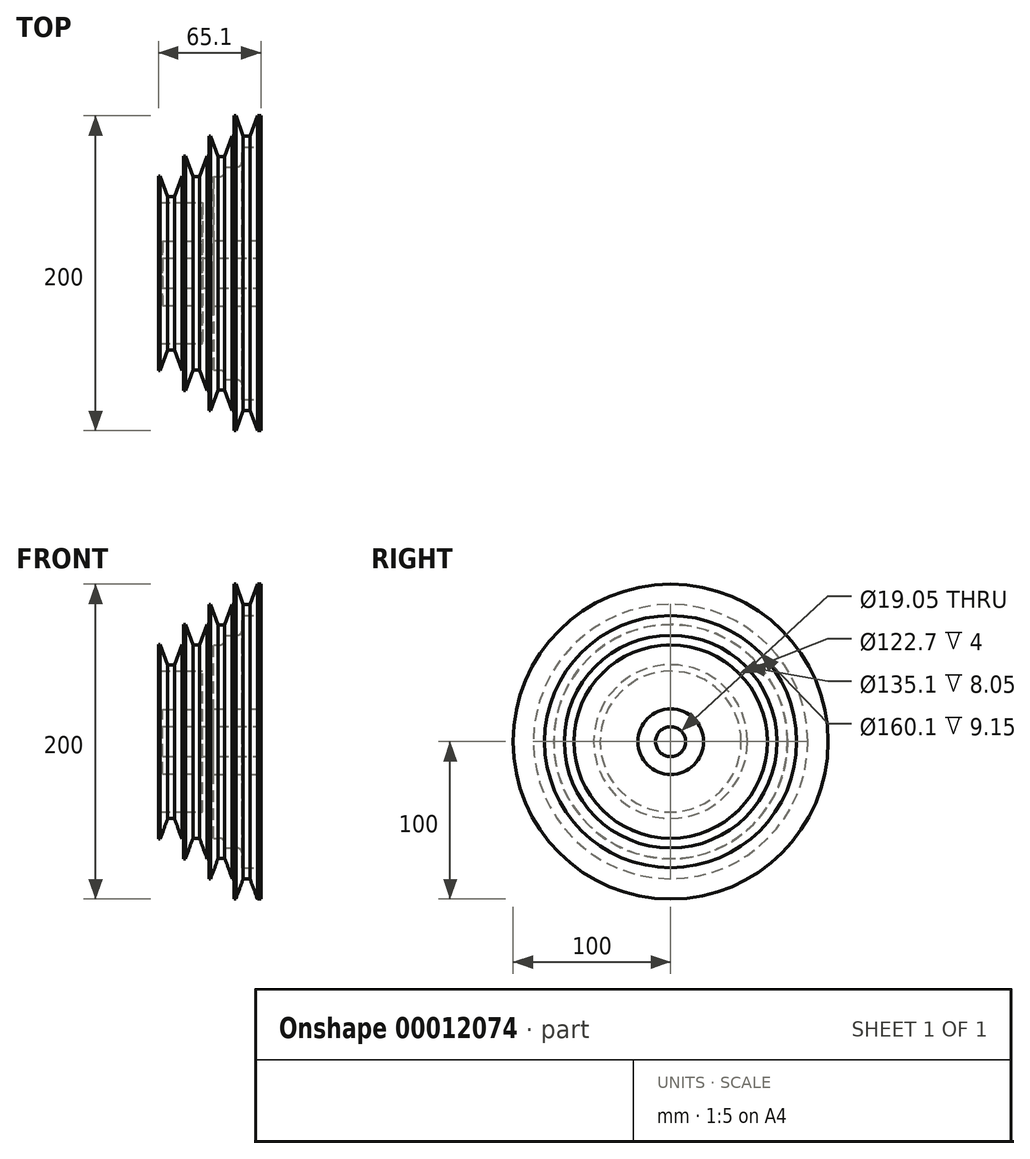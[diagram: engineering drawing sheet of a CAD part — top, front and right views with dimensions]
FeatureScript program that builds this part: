
annotation { "Feature Type Name" : "Feature", "Feature Type Description" : "" }
export const myFeature = defineFeature(function(context is Context, id is Id, definition is map)
    precondition{}
    {
        {
            var Q0;
            Q0=qCreatedBy(makeId("Front.planeOp"),FACE);
            var sketch = newSketch(context, id + "F0", { "sketchPlane" : qUnion([Q0])});
            skLineSegment(sketch, "E0", {"start": v(-43.25, 31.5) * mm, "end": v(-38.95, 31.5) * mm});
            skLineSegment(sketch, "E1", {"start": v(-43.25, 31.5) * mm, "end": v(-47.95, 44.4) * mm});
            skLineSegment(sketch, "E2", {"start": v(-38.95, 31.5) * mm, "end": v(-34.25, 44.4) * mm});
            skLineSegment(sketch, "E3", {"start": v(-49.1, 44.4) * mm, "end": v(-47.95, 44.4) * mm});
            skLineSegment(sketch, "E4.trimOffspring", {"start": v(-34.25, 44.4) * mm, "end": v(-33.1, 44.4) * mm});
            skPoint(sketch, "E5.start.orphan", {"position": v(-41.1, 31.5) * mm});
            skPoint(sketch, "E6.orphan", {"position": v(-41.1, 44.4) * mm});
            skLineSegment(sketch, "E7", {"start": v(-59.25, 18.85) * mm, "end": v(-54.95, 18.85) * mm});
            skLineSegment(sketch, "E8", {"start": v(-59.25, 18.85) * mm, "end": v(-63.95, 31.75) * mm});
            skLineSegment(sketch, "E9", {"start": v(-54.95, 18.85) * mm, "end": v(-50.25, 31.75) * mm});
            skLineSegment(sketch, "E10", {"start": v(-65.1, 31.75) * mm, "end": v(-63.95, 31.75) * mm});
            skLineSegment(sketch, "E11.trimOffspring", {"start": v(-50.25, 31.75) * mm, "end": v(-49.1, 31.75) * mm});
            skPoint(sketch, "E12.start.orphan", {"position": v(-57.1, 18.85) * mm});
            skPoint(sketch, "E13.orphan", {"position": v(-57.1, 31.75) * mm});
            skLineSegment(sketch, "E14", {"start": v(-11.25, 57.1) * mm, "end": v(-6.95, 57.1) * mm});
            skLineSegment(sketch, "E15", {"start": v(-11.25, 57.1) * mm, "end": v(-15.94, 70) * mm});
            skLineSegment(sketch, "E16", {"start": v(-6.95, 57.1) * mm, "end": v(-2.25, 70) * mm});
            skLineSegment(sketch, "E17", {"start": v(-17.1, 70) * mm, "end": v(-15.94, 70) * mm});
            skPoint(sketch, "E18.start.orphan", {"position": v(-9.1, 57.1) * mm});
            skPoint(sketch, "E19.orphan", {"position": v(-9.1, 70) * mm});
            skLineSegment(sketch, "E20", {"start": v(-27.25, 44.2) * mm, "end": v(-22.95, 44.2) * mm});
            skLineSegment(sketch, "E21", {"start": v(-27.25, 44.2) * mm, "end": v(-31.95, 57.1) * mm});
            skLineSegment(sketch, "E22", {"start": v(-22.95, 44.2) * mm, "end": v(-18.25, 57.1) * mm});
            skLineSegment(sketch, "E23", {"start": v(-33.1, 57.1) * mm, "end": v(-31.95, 57.1) * mm});
            skLineSegment(sketch, "E24.trimOffspring", {"start": v(-18.25, 57.1) * mm, "end": v(-17.1, 57.1) * mm});
            skPoint(sketch, "E25.start.orphan", {"position": v(-25.1, 44.2) * mm});
            skPoint(sketch, "E26.orphan", {"position": v(-25.1, 57.1) * mm});
            skLineSegment(sketch, "E27", {"start": v(-65.1, 31.75) * mm, "end": v(-65.1, 14.75) * mm});
            skLineSegment(sketch, "E28", {"start": v(-49.1, 44.4) * mm, "end": v(-49.1, 31.75) * mm});
            skLineSegment(sketch, "E29", {"start": v(-33.1, 57.1) * mm, "end": v(-33.1, 44.4) * mm});
            skLineSegment(sketch, "E30", {"start": v(-17.1, 70) * mm, "end": v(-17.1, 57.1) * mm});
            skLineSegment(sketch, "E31", {"start": v(-2.25, 70) * mm, "end": v(0, 70) * mm});
            skLineSegment(sketch, "E32.0", {"start": v(-1.4, -20.48) * mm, "end": v(-62.5, -20.48) * mm});
            skLineSegment(sketch, "E33.0", {"start": v(0, -30) * mm, "end": v(-65.1, -30) * mm, "construction": true});
            skLineSegment(sketch, "E34", {"start": v(-65.1, 14.75) * mm, "end": v(-37, 14.75) * mm});
            skLineSegment(sketch, "E35", {"start": v(-37, -9.5) * mm, "end": v(-62.5, -9.5) * mm});
            skLineSegment(sketch, "E36", {"start": v(-37, 14.75) * mm, "end": v(-37, -9.5) * mm});
            skLineSegment(sketch, "E37", {"start": v(-62.5, -9.5) * mm, "end": v(-62.5, -20.48) * mm});
            skLineSegment(sketch, "E38", {"start": v(-1.4, -9.15) * mm, "end": v(-30.2, -9.15) * mm});
            skLineSegment(sketch, "E39", {"start": v(-30.2, -9.15) * mm, "end": v(-30.2, 31.35) * mm});
            skLineSegment(sketch, "E40", {"start": v(-30.2, 31.35) * mm, "end": v(-26.2, 31.35) * mm});
            skLineSegment(sketch, "E41.trimOffspring", {"start": v(0, 53.05) * mm, "end": v(0, 70) * mm});
            skLineSegment(sketch, "E42", {"start": v(-1.4, -9.15) * mm, "end": v(-1.4, -20.48) * mm});
            skPoint(sketch, "E43.left.end.orphan", {"position": v(0, -9.15) * mm});
            skLineSegment(sketch, "E44", {"start": v(-23.2, 34.35) * mm, "end": v(-23.2, 37.55) * mm});
            skLineSegment(sketch, "E45", {"start": v(-23.2, 37.55) * mm, "end": v(-15.15, 37.55) * mm});
            skLineSegment(sketch, "E46", {"start": v(-12.15, 40.55) * mm, "end": v(-12.15, 50.05) * mm});
            skLineSegment(sketch, "E47", {"start": v(-12.15, 50.05) * mm, "end": v(-3, 50.05) * mm});
            skPoint(sketch, "E48.orphan", {"position": v(0, 31.35) * mm});
            skPoint(sketch, "E49.visualSharp", {"position": v(-23.2, 31.35) * mm});
            skArc(sketch, "E49.filletArc", {"start": v(-26.2, 31.35) * mm, "mid": v(-24.08, 32.23) * mm, "end": v(-23.2, 34.35) * mm});
            skPoint(sketch, "E50.visualSharp", {"position": v(-12.15, 37.55) * mm});
            skArc(sketch, "E50.filletArc", {"start": v(-15.15, 37.55) * mm, "mid": v(-13.03, 38.43) * mm, "end": v(-12.15, 40.55) * mm});
            skPoint(sketch, "E51.visualSharp", {"position": v(0, 50.05) * mm});
            skArc(sketch, "E51.filletArc", {"start": v(-3, 50.05) * mm, "mid": v(-0.88, 50.93) * mm, "end": v(0, 53.05) * mm});
            skSolve(sketch);
        }
        {
            var Q0;
            Q0=qSketchRegion(id+"F0",true);
            var Q1;
            Q1=sQuery(id+"F0.wireOp",EDGE,"E33.0");
            revolve(context, id + "F1", {"entities" : qUnion([Q0]), "axis" : qUnion([Q1]), "revolveType" : RevolveType.FULL});
        }
    });
